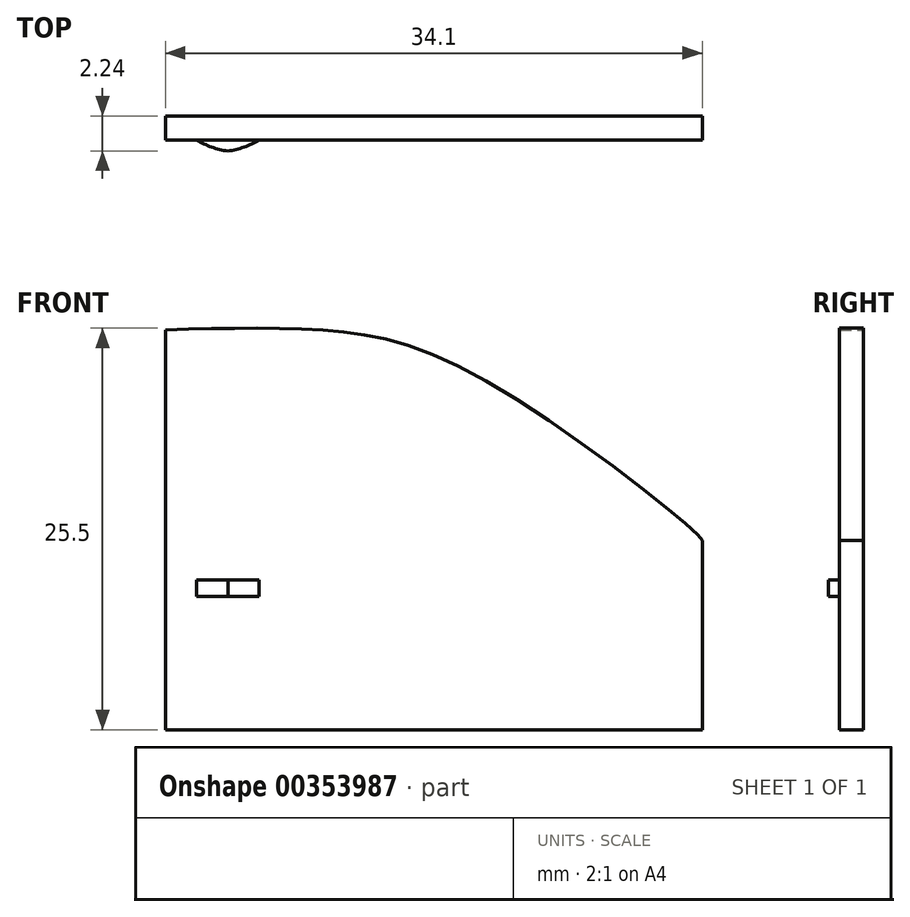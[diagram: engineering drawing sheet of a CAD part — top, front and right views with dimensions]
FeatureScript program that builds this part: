
annotation { "Feature Type Name" : "Feature", "Feature Type Description" : "" }
export const myFeature = defineFeature(function(context is Context, id is Id, definition is map)
    precondition{}
    {
        {
            var Q0;
            Q0=qCreatedBy(makeId("Front.planeOp"),FACE);
            var sketch = newSketch(context, id + "F0", { "sketchPlane" : qUnion([Q0])});
            skLineSegment(sketch, "E0", {"start": v(-20.5, 13.38) * mm, "end": v(-20.5, -12.02) * mm});
            skFitSpline(sketch, "E1", {"points": [v(-20.5, 13.38) * mm, v(-10.84, 13.38) * mm, v(0, 10.05) * mm, v(13.6, 0) * mm, v(13.4, 0) * mm], "startDerivative": vector(35.26, 0.94) * mm, "endDerivative": vector(-7.23, 1.73) * mm});
            skLineSegment(sketch, "E2", {"start": v(-20.5, -12.02) * mm, "end": v(13.6, -12.02) * mm});
            skLineSegment(sketch, "E3", {"start": v(13.6, -12.02) * mm, "end": v(13.6, 0) * mm});
            skLineSegment(sketch, "E4", {"start": v(13.6, 0) * mm, "end": v(-20.5, 0) * mm});
            skLineSegment(sketch, "E5.bottom", {"start": v(-18.52, -2.5) * mm, "end": v(-14.55, -2.5) * mm});
            skLineSegment(sketch, "E5.top", {"start": v(-18.52, -3.55) * mm, "end": v(-14.55, -3.55) * mm});
            skLineSegment(sketch, "E5.left", {"start": v(-18.52, -2.5) * mm, "end": v(-18.52, -3.55) * mm});
            skLineSegment(sketch, "E5.right", {"start": v(-14.55, -2.5) * mm, "end": v(-14.55, -3.55) * mm});
            skSolve(sketch);
        }
        {
            var Q0;
            {var subQ0=sQuery(id+"F0.wireOp",EDGE,"nOc6ndhr-CEWs-2MWZ-xoqL-Ha6ft26fFmGs");var subQ1=sQuery(id+"F0.wireOp",EDGE,"E4");var subQ2=makeQuery(id+"F0.imprint","INTERSECT",VERTEX,{"derivedFrom":[subQ1,subQ0]});Q0=makeQuery(id+"F0.imprint","IMPRINT",FACE,{"disambiguationData":[TD([[makeQuery(id+"F0.imprint","IMPRINT",EDGE,{"disambiguationData":[TD([[subQ2,1.0]])],"derivedFrom":subQ1}),-1.0]])]});}
            var Q1;
            {var subQ0=sQuery(id+"F0.wireOp",EDGE,"8BRhcVoK-4ZSY-d9QQ-jCl1-HMr4gjxtuWuF");var subQ1=sQuery(id+"F0.wireOp",EDGE,"XEESbgik-Cwhb-kf8o-8iuY-mVMpAegihUSW");var subQ2=makeQuery(id+"F0.imprint","INTERSECT",VERTEX,{"derivedFrom":[subQ1,subQ0]});Q1=makeQuery(id+"F0.imprint","IMPRINT",FACE,{"disambiguationData":[TD([[makeQuery(id+"F0.imprint","IMPRINT",EDGE,{"disambiguationData":[TD([[subQ2,-1.0]])],"derivedFrom":subQ1}),1.0]])]});}
            var Q2;
            {var subQ0=sQuery(id+"F0.wireOp",EDGE,"pVUgloD8-eKz4-1CY4-ZZar-P1BLLFPWEFhO");var subQ1=sQuery(id+"F0.wireOp",EDGE,"E1");var subQ2=makeQuery(id+"F0.imprint","INTERSECT",VERTEX,{"derivedFrom":[subQ1,subQ0]});Q2=makeQuery(id+"F0.imprint","IMPRINT",FACE,{"disambiguationData":[TD([[makeQuery(id+"F0.imprint","IMPRINT",EDGE,{"disambiguationData":[TD([[subQ2,1.0]])],"derivedFrom":subQ1}),-1.0]])]});}
            var Q3;
            {var subQ0=sQuery(id+"F0.wireOp",EDGE,"MwFNBffj-ykpu-HGD8-Ynrz-I9LzijhiDSCR");var subQ1=sQuery(id+"F0.wireOp",EDGE,"CX13CTTp-Oqm4-u2hn-fSbW-toaxqpDcd6P2");var subQ2=makeQuery(id+"F0.imprint","INTERSECT",VERTEX,{"derivedFrom":[subQ1,subQ0]});Q3=makeQuery(id+"F0.imprint","IMPRINT",FACE,{"disambiguationData":[TD([[makeQuery(id+"F0.imprint","IMPRINT",EDGE,{"disambiguationData":[TD([[subQ2,-1.0]])],"derivedFrom":subQ1}),1.0]])]});}
            var Q4;
            {var subQ0=sQuery(id+"F0.wireOp",EDGE,"8BRhcVoK-4ZSY-d9QQ-jCl1-HMr4gjxtuWuF");var subQ1=sQuery(id+"F0.wireOp",EDGE,"E0");var subQ2=makeQuery(id+"F0.imprint","INTERSECT",VERTEX,{"derivedFrom":[subQ1,subQ0]});Q4=makeQuery(id+"F0.imprint","IMPRINT",FACE,{"disambiguationData":[TD([[makeQuery(id+"F0.imprint","IMPRINT",EDGE,{"disambiguationData":[TD([[subQ2,-1.0]])],"derivedFrom":subQ1}),1.0]])]});}
            var Q5;
            {var subQ0=sQuery(id+"F0.wireOp",EDGE,"ATKICQp3-aMIP-nDqe-qzJb-LSgsvSxOWsnF");var subQ1=sQuery(id+"F0.wireOp",EDGE,"CX13CTTp-Oqm4-u2hn-fSbW-toaxqpDcd6P2");var subQ2=makeQuery(id+"F0.imprint","INTERSECT",VERTEX,{"derivedFrom":[subQ1,subQ0]});Q5=makeQuery(id+"F0.imprint","IMPRINT",FACE,{"disambiguationData":[TD([[makeQuery(id+"F0.imprint","IMPRINT",EDGE,{"disambiguationData":[TD([[subQ2,-1.0]])],"derivedFrom":subQ1}),1.0]])]});}
            var Q6;
            {var subQ0=sQuery(id+"F0.wireOp",EDGE,"MwFNBffj-ykpu-HGD8-Ynrz-I9LzijhiDSCR");var subQ1=sQuery(id+"F0.wireOp",EDGE,"XEESbgik-Cwhb-kf8o-8iuY-mVMpAegihUSW");var subQ2=makeQuery(id+"F0.imprint","INTERSECT",VERTEX,{"derivedFrom":[subQ1,subQ0]});Q6=makeQuery(id+"F0.imprint","IMPRINT",FACE,{"disambiguationData":[TD([[makeQuery(id+"F0.imprint","IMPRINT",EDGE,{"disambiguationData":[TD([[subQ2,-1.0]])],"derivedFrom":subQ1}),-1.0]])]});}
            var Q7;
            {var subQ0=sQuery(id+"F0.wireOp",EDGE,"XdJaFeX5-YPTi-reul-S0qf-juZpPkdLSGOt");var subQ1=sQuery(id+"F0.wireOp",EDGE,"XEESbgik-Cwhb-kf8o-8iuY-mVMpAegihUSW");var subQ2=makeQuery(id+"F0.imprint","INTERSECT",VERTEX,{"derivedFrom":[subQ1,subQ0]});Q7=makeQuery(id+"F0.imprint","IMPRINT",FACE,{"disambiguationData":[TD([[makeQuery(id+"F0.imprint","IMPRINT",EDGE,{"disambiguationData":[TD([[subQ2,-1.0]])],"derivedFrom":subQ1}),-1.0]])]});}
            var Q8;
            {var subQ0=sQuery(id+"F0.wireOp",EDGE,"ATKICQp3-aMIP-nDqe-qzJb-LSgsvSxOWsnF");var subQ1=sQuery(id+"F0.wireOp",EDGE,"E0");var subQ2=makeQuery(id+"F0.imprint","INTERSECT",VERTEX,{"derivedFrom":[subQ1,subQ0]});Q8=makeQuery(id+"F0.imprint","IMPRINT",FACE,{"disambiguationData":[TD([[makeQuery(id+"F0.imprint","IMPRINT",EDGE,{"disambiguationData":[TD([[subQ2,1.0]])],"derivedFrom":subQ1}),1.0]])]});}
            var Q9;
            {var subQ0=sQuery(id+"F0.wireOp",EDGE,"ATKICQp3-aMIP-nDqe-qzJb-LSgsvSxOWsnF");var subQ1=sQuery(id+"F0.wireOp",EDGE,"E0");var subQ2=makeQuery(id+"F0.imprint","INTERSECT",VERTEX,{"derivedFrom":[subQ1,subQ0]});Q9=makeQuery(id+"F0.imprint","IMPRINT",FACE,{"disambiguationData":[TD([[makeQuery(id+"F0.imprint","IMPRINT",EDGE,{"disambiguationData":[TD([[subQ2,-1.0]])],"derivedFrom":subQ1}),1.0]])]});}
            var Q10;
            {var subQ0=sQuery(id+"F0.wireOp",EDGE,"8BRhcVoK-4ZSY-d9QQ-jCl1-HMr4gjxtuWuF");var subQ1=sQuery(id+"F0.wireOp",EDGE,"yqfY02yN-hyVq-32UO-ZW3n-jwWNOL1hSBTT");var subQ2=makeQuery(id+"F0.imprint","INTERSECT",VERTEX,{"derivedFrom":[subQ1,subQ0]});Q10=makeQuery(id+"F0.imprint","IMPRINT",FACE,{"disambiguationData":[TD([[makeQuery(id+"F0.imprint","IMPRINT",EDGE,{"disambiguationData":[TD([[subQ2,-1.0]])],"derivedFrom":subQ1}),1.0]])]});}
            var Q11;
            {var subQ0=sQuery(id+"F0.wireOp",EDGE,"XdJaFeX5-YPTi-reul-S0qf-juZpPkdLSGOt");var subQ1=sQuery(id+"F0.wireOp",EDGE,"CX13CTTp-Oqm4-u2hn-fSbW-toaxqpDcd6P2");var subQ2=makeQuery(id+"F0.imprint","INTERSECT",VERTEX,{"derivedFrom":[subQ1,subQ0]});Q11=makeQuery(id+"F0.imprint","IMPRINT",FACE,{"disambiguationData":[TD([[makeQuery(id+"F0.imprint","IMPRINT",EDGE,{"disambiguationData":[TD([[subQ2,-1.0]])],"derivedFrom":subQ1}),1.0]])]});}
            var Q12;
            {var subQ1=sQuery(id+"F0.wireOp",EDGE,"E4");var subQ5=sQuery(id+"F0.wireOp",EDGE,"E1");var subQ6=makeQuery(id+"F0.imprint","INTERSECT",VERTEX,{"derivedFrom":[subQ5,subQ1]});Q12=makeQuery(id+"F0.imprint","IMPRINT",FACE,{"disambiguationData":[TD([[makeQuery(id+"F0.imprint","IMPRINT",EDGE,{"disambiguationData":[TD([[subQ6,-1.0]])],"derivedFrom":subQ1}),-1.0]])]});}
            var Q13;
            {var subQ0=sQuery(id+"F0.wireOp",EDGE,"ONkRjr3D-5ST7-0iBJ-Hq3S-bNWUPIyy0om7");var subQ1=sQuery(id+"F0.wireOp",EDGE,"E0");var subQ2=makeQuery(id+"F0.imprint","INTERSECT",VERTEX,{"derivedFrom":[subQ1,subQ0]});Q13=makeQuery(id+"F0.imprint","IMPRINT",FACE,{"disambiguationData":[TD([[makeQuery(id+"F0.imprint","IMPRINT",EDGE,{"disambiguationData":[TD([[subQ2,-1.0]])],"derivedFrom":subQ1}),1.0]])]});}
            var Q14;
            {var subQ0=sQuery(id+"F0.wireOp",EDGE,"gvejoAXR-BtHd-F8Sq-gFUB-eTjeAkh79I8N");var subQ1=sQuery(id+"F0.wireOp",EDGE,"PEqbovu0-osZd-sZTq-e7nW-4YB9cD3i2QqJ");var subQ2=makeQuery(id+"F0.imprint","INTERSECT",VERTEX,{"derivedFrom":[subQ1,subQ0]});Q14=makeQuery(id+"F0.imprint","IMPRINT",FACE,{"disambiguationData":[TD([[makeQuery(id+"F0.imprint","IMPRINT",EDGE,{"disambiguationData":[TD([[subQ2,-1.0]])],"derivedFrom":subQ1}),1.0]])]});}
            var Q15;
            {var subQ0=sQuery(id+"F0.wireOp",EDGE,"XEESbgik-Cwhb-kf8o-8iuY-mVMpAegihUSW");var subQ1=sQuery(id+"F0.wireOp",EDGE,"E1");var subQ2=makeQuery(id+"F0.imprint","INTERSECT",VERTEX,{"derivedFrom":[subQ1,subQ0]});Q15=makeQuery(id+"F0.imprint","IMPRINT",FACE,{"disambiguationData":[TD([[makeQuery(id+"F0.imprint","IMPRINT",EDGE,{"disambiguationData":[TD([[subQ2,-1.0]])],"derivedFrom":subQ1}),-1.0]])]});}
            var Q16;
            {var subQ0=sQuery(id+"F0.wireOp",EDGE,"ONkRjr3D-5ST7-0iBJ-Hq3S-bNWUPIyy0om7");var subQ1=sQuery(id+"F0.wireOp",EDGE,"V6lheY5w-4WYN-of84-aoai-MSi1px95FpYR");var subQ2=makeQuery(id+"F0.imprint","INTERSECT",VERTEX,{"derivedFrom":[subQ1,subQ0]});Q16=makeQuery(id+"F0.imprint","IMPRINT",FACE,{"disambiguationData":[TD([[makeQuery(id+"F0.imprint","IMPRINT",EDGE,{"disambiguationData":[TD([[subQ2,-1.0]])],"derivedFrom":subQ1}),1.0]])]});}
            var Q17;
            {var subQ0=sQuery(id+"F0.wireOp",EDGE,"8BRhcVoK-4ZSY-d9QQ-jCl1-HMr4gjxtuWuF");var subQ1=sQuery(id+"F0.wireOp",EDGE,"V6lheY5w-4WYN-of84-aoai-MSi1px95FpYR");var subQ2=makeQuery(id+"F0.imprint","INTERSECT",VERTEX,{"derivedFrom":[subQ1,subQ0]});Q17=makeQuery(id+"F0.imprint","IMPRINT",FACE,{"disambiguationData":[TD([[makeQuery(id+"F0.imprint","IMPRINT",EDGE,{"disambiguationData":[TD([[subQ2,-1.0]])],"derivedFrom":subQ1}),1.0]])]});}
            var Q18;
            {var subQ0=sQuery(id+"F0.wireOp",EDGE,"ATKICQp3-aMIP-nDqe-qzJb-LSgsvSxOWsnF");var subQ1=sQuery(id+"F0.wireOp",EDGE,"V6lheY5w-4WYN-of84-aoai-MSi1px95FpYR");var subQ2=makeQuery(id+"F0.imprint","INTERSECT",VERTEX,{"derivedFrom":[subQ1,subQ0]});Q18=makeQuery(id+"F0.imprint","IMPRINT",FACE,{"disambiguationData":[TD([[makeQuery(id+"F0.imprint","IMPRINT",EDGE,{"disambiguationData":[TD([[subQ2,-1.0]])],"derivedFrom":subQ1}),1.0]])]});}
            var Q19;
            {var subQ0=sQuery(id+"F0.wireOp",EDGE,"ONkRjr3D-5ST7-0iBJ-Hq3S-bNWUPIyy0om7");var subQ1=sQuery(id+"F0.wireOp",EDGE,"yqfY02yN-hyVq-32UO-ZW3n-jwWNOL1hSBTT");var subQ2=makeQuery(id+"F0.imprint","INTERSECT",VERTEX,{"derivedFrom":[subQ1,subQ0]});Q19=makeQuery(id+"F0.imprint","IMPRINT",FACE,{"disambiguationData":[TD([[makeQuery(id+"F0.imprint","IMPRINT",EDGE,{"disambiguationData":[TD([[subQ2,-1.0]])],"derivedFrom":subQ1}),1.0]])]});}
            var Q20;
            {var subQ0=sQuery(id+"F0.wireOp",EDGE,"MwFNBffj-ykpu-HGD8-Ynrz-I9LzijhiDSCR");var subQ1=sQuery(id+"F0.wireOp",EDGE,"E0");var subQ2=makeQuery(id+"F0.imprint","INTERSECT",VERTEX,{"derivedFrom":[subQ1,subQ0]});Q20=makeQuery(id+"F0.imprint","IMPRINT",FACE,{"disambiguationData":[TD([[makeQuery(id+"F0.imprint","IMPRINT",EDGE,{"disambiguationData":[TD([[subQ2,-1.0]])],"derivedFrom":subQ1}),1.0]])]});}
            var Q21;
            {var subQ0=sQuery(id+"F0.wireOp",EDGE,"XdJaFeX5-YPTi-reul-S0qf-juZpPkdLSGOt");var subQ1=sQuery(id+"F0.wireOp",EDGE,"E1");var subQ2=makeQuery(id+"F0.imprint","INTERSECT",VERTEX,{"derivedFrom":[subQ1,subQ0]});Q21=makeQuery(id+"F0.imprint","IMPRINT",FACE,{"disambiguationData":[TD([[makeQuery(id+"F0.imprint","IMPRINT",EDGE,{"disambiguationData":[TD([[subQ2,-1.0]])],"derivedFrom":subQ1}),-1.0]])]});}
            var Q22;
            {var subQ0=sQuery(id+"F0.wireOp",EDGE,"Okv4lNKS-qbql-g7VV-lbg5-xwRJb0XAX9qC");var subQ1=sQuery(id+"F0.wireOp",EDGE,"E0");var subQ2=makeQuery(id+"F0.imprint","INTERSECT",VERTEX,{"derivedFrom":[subQ1,subQ0]});Q22=makeQuery(id+"F0.imprint","IMPRINT",FACE,{"disambiguationData":[TD([[makeQuery(id+"F0.imprint","IMPRINT",EDGE,{"disambiguationData":[TD([[subQ2,-1.0]])],"derivedFrom":subQ1}),1.0]])]});}
            var Q23;
            {var subQ0=sQuery(id+"F0.wireOp",EDGE,"XdJaFeX5-YPTi-reul-S0qf-juZpPkdLSGOt");var subQ1=sQuery(id+"F0.wireOp",EDGE,"E0");var subQ2=makeQuery(id+"F0.imprint","INTERSECT",VERTEX,{"derivedFrom":[subQ1,subQ0]});Q23=makeQuery(id+"F0.imprint","IMPRINT",FACE,{"disambiguationData":[TD([[makeQuery(id+"F0.imprint","IMPRINT",EDGE,{"disambiguationData":[TD([[subQ2,-1.0]])],"derivedFrom":subQ1}),1.0]])]});}
            var Q24;
            {var subQ0=sQuery(id+"F0.wireOp",EDGE,"gvejoAXR-BtHd-F8Sq-gFUB-eTjeAkh79I8N");var subQ1=sQuery(id+"F0.wireOp",EDGE,"CX13CTTp-Oqm4-u2hn-fSbW-toaxqpDcd6P2");var subQ2=makeQuery(id+"F0.imprint","INTERSECT",VERTEX,{"derivedFrom":[subQ1,subQ0]});Q24=makeQuery(id+"F0.imprint","IMPRINT",FACE,{"disambiguationData":[TD([[makeQuery(id+"F0.imprint","IMPRINT",EDGE,{"disambiguationData":[TD([[subQ2,-1.0]])],"derivedFrom":subQ1}),1.0]])]});}
            var Q25;
            {var subQ0=sQuery(id+"F0.wireOp",EDGE,"8BRhcVoK-4ZSY-d9QQ-jCl1-HMr4gjxtuWuF");var subQ1=sQuery(id+"F0.wireOp",EDGE,"XEESbgik-Cwhb-kf8o-8iuY-mVMpAegihUSW");var subQ2=makeQuery(id+"F0.imprint","INTERSECT",VERTEX,{"derivedFrom":[subQ1,subQ0]});Q25=makeQuery(id+"F0.imprint","IMPRINT",FACE,{"disambiguationData":[TD([[makeQuery(id+"F0.imprint","IMPRINT",EDGE,{"disambiguationData":[TD([[subQ2,-1.0]])],"derivedFrom":subQ1}),-1.0]])]});}
            var Q26;
            {var subQ0=sQuery(id+"F0.wireOp",EDGE,"Okv4lNKS-qbql-g7VV-lbg5-xwRJb0XAX9qC");var subQ1=sQuery(id+"F0.wireOp",EDGE,"E1");var subQ2=makeQuery(id+"F0.imprint","INTERSECT",VERTEX,{"derivedFrom":[subQ1,subQ0]});Q26=makeQuery(id+"F0.imprint","IMPRINT",FACE,{"disambiguationData":[TD([[makeQuery(id+"F0.imprint","IMPRINT",EDGE,{"disambiguationData":[TD([[subQ2,-1.0]])],"derivedFrom":subQ1}),-1.0]])]});}
            var Q27;
            {var subQ1=sQuery(id+"F0.wireOp",EDGE,"E1");var subQ5=sQuery(id+"F0.wireOp",EDGE,"fXT5uzoG-60Do-cvdt-QS0y-XCeuEJHzKh4q");var subQ6=makeQuery(id+"F0.imprint","INTERSECT",VERTEX,{"derivedFrom":[subQ1,subQ5]});Q27=makeQuery(id+"F0.imprint","IMPRINT",FACE,{"disambiguationData":[TD([[makeQuery(id+"F0.imprint","IMPRINT",EDGE,{"disambiguationData":[TD([[subQ6,1.0]])],"derivedFrom":subQ1}),-1.0]])]});}
            var Q28;
            {var subQ0=sQuery(id+"F0.wireOp",EDGE,"BWVHoUEd-ofww-dxFT-yNqJ-OOrmRnXLyRp3");var subQ1=sQuery(id+"F0.wireOp",EDGE,"E0");var subQ2=makeQuery(id+"F0.imprint","INTERSECT",VERTEX,{"derivedFrom":[subQ1,subQ0]});Q28=makeQuery(id+"F0.imprint","IMPRINT",FACE,{"disambiguationData":[TD([[makeQuery(id+"F0.imprint","IMPRINT",EDGE,{"disambiguationData":[TD([[subQ2,-1.0]])],"derivedFrom":subQ1}),1.0]])]});}
            var Q29;
            {var subQ0=sQuery(id+"F0.wireOp",EDGE,"E4");var subQ1=sQuery(id+"F0.wireOp",EDGE,"E0");var subQ2=makeQuery(id+"F0.imprint","INTERSECT",VERTEX,{"derivedFrom":[subQ1,subQ0]});Q29=makeQuery(id+"F0.imprint","IMPRINT",FACE,{"disambiguationData":[TD([[makeQuery(id+"F0.imprint","IMPRINT",EDGE,{"disambiguationData":[TD([[subQ2,1.0]])],"derivedFrom":subQ1}),1.0]])]});}
            var Q30;
            {var subQ0=sQuery(id+"F0.wireOp",EDGE,"Okv4lNKS-qbql-g7VV-lbg5-xwRJb0XAX9qC");var subQ1=sQuery(id+"F0.wireOp",EDGE,"XEESbgik-Cwhb-kf8o-8iuY-mVMpAegihUSW");var subQ2=makeQuery(id+"F0.imprint","INTERSECT",VERTEX,{"derivedFrom":[subQ1,subQ0]});Q30=makeQuery(id+"F0.imprint","IMPRINT",FACE,{"disambiguationData":[TD([[makeQuery(id+"F0.imprint","IMPRINT",EDGE,{"disambiguationData":[TD([[subQ2,-1.0]])],"derivedFrom":subQ1}),1.0]])]});}
            var Q31;
            {var subQ0=sQuery(id+"F0.wireOp",EDGE,"BWVHoUEd-ofww-dxFT-yNqJ-OOrmRnXLyRp3");var subQ1=sQuery(id+"F0.wireOp",EDGE,"yqfY02yN-hyVq-32UO-ZW3n-jwWNOL1hSBTT");var subQ2=makeQuery(id+"F0.imprint","INTERSECT",VERTEX,{"derivedFrom":[subQ1,subQ0]});Q31=makeQuery(id+"F0.imprint","IMPRINT",FACE,{"disambiguationData":[TD([[makeQuery(id+"F0.imprint","IMPRINT",EDGE,{"disambiguationData":[TD([[subQ2,-1.0]])],"derivedFrom":subQ1}),1.0]])]});}
            var Q32;
            {var subQ0=sQuery(id+"F0.wireOp",EDGE,"ONkRjr3D-5ST7-0iBJ-Hq3S-bNWUPIyy0om7");var subQ1=sQuery(id+"F0.wireOp",EDGE,"E1");var subQ2=makeQuery(id+"F0.imprint","INTERSECT",VERTEX,{"derivedFrom":[subQ1,subQ0]});Q32=makeQuery(id+"F0.imprint","IMPRINT",FACE,{"disambiguationData":[TD([[makeQuery(id+"F0.imprint","IMPRINT",EDGE,{"disambiguationData":[TD([[subQ2,-1.0]])],"derivedFrom":subQ1}),-1.0]])]});}
            var Q33;
            {var subQ0=sQuery(id+"F0.wireOp",EDGE,"BWVHoUEd-ofww-dxFT-yNqJ-OOrmRnXLyRp3");var subQ1=sQuery(id+"F0.wireOp",EDGE,"CX13CTTp-Oqm4-u2hn-fSbW-toaxqpDcd6P2");var subQ2=makeQuery(id+"F0.imprint","INTERSECT",VERTEX,{"derivedFrom":[subQ1,subQ0]});Q33=makeQuery(id+"F0.imprint","IMPRINT",FACE,{"disambiguationData":[TD([[makeQuery(id+"F0.imprint","IMPRINT",EDGE,{"disambiguationData":[TD([[subQ2,-1.0]])],"derivedFrom":subQ1}),1.0]])]});}
            var Q34;
            {var subQ0=sQuery(id+"F0.wireOp",EDGE,"Okv4lNKS-qbql-g7VV-lbg5-xwRJb0XAX9qC");var subQ1=sQuery(id+"F0.wireOp",EDGE,"nOc6ndhr-CEWs-2MWZ-xoqL-Ha6ft26fFmGs");var subQ2=makeQuery(id+"F0.imprint","INTERSECT",VERTEX,{"derivedFrom":[subQ1,subQ0]});Q34=makeQuery(id+"F0.imprint","IMPRINT",FACE,{"disambiguationData":[TD([[makeQuery(id+"F0.imprint","IMPRINT",EDGE,{"disambiguationData":[TD([[subQ2,-1.0]])],"derivedFrom":subQ1}),1.0]])]});}
            var Q35;
            {var subQ0=sQuery(id+"F0.wireOp",EDGE,"BWVHoUEd-ofww-dxFT-yNqJ-OOrmRnXLyRp3");var subQ1=sQuery(id+"F0.wireOp",EDGE,"nOc6ndhr-CEWs-2MWZ-xoqL-Ha6ft26fFmGs");var subQ2=makeQuery(id+"F0.imprint","INTERSECT",VERTEX,{"derivedFrom":[subQ1,subQ0]});Q35=makeQuery(id+"F0.imprint","IMPRINT",FACE,{"disambiguationData":[TD([[makeQuery(id+"F0.imprint","IMPRINT",EDGE,{"disambiguationData":[TD([[subQ2,-1.0]])],"derivedFrom":subQ1}),1.0]])]});}
            var Q36;
            {var subQ0=sQuery(id+"F0.wireOp",EDGE,"ONkRjr3D-5ST7-0iBJ-Hq3S-bNWUPIyy0om7");var subQ1=sQuery(id+"F0.wireOp",EDGE,"PEqbovu0-osZd-sZTq-e7nW-4YB9cD3i2QqJ");var subQ2=makeQuery(id+"F0.imprint","INTERSECT",VERTEX,{"derivedFrom":[subQ1,subQ0]});Q36=makeQuery(id+"F0.imprint","IMPRINT",FACE,{"disambiguationData":[TD([[makeQuery(id+"F0.imprint","IMPRINT",EDGE,{"disambiguationData":[TD([[subQ2,-1.0]])],"derivedFrom":subQ1}),1.0]])]});}
            var Q37;
            {var subQ0=sQuery(id+"F0.wireOp",EDGE,"gvejoAXR-BtHd-F8Sq-gFUB-eTjeAkh79I8N");var subQ1=sQuery(id+"F0.wireOp",EDGE,"XEESbgik-Cwhb-kf8o-8iuY-mVMpAegihUSW");var subQ2=makeQuery(id+"F0.imprint","INTERSECT",VERTEX,{"derivedFrom":[subQ1,subQ0]});Q37=makeQuery(id+"F0.imprint","IMPRINT",FACE,{"disambiguationData":[TD([[makeQuery(id+"F0.imprint","IMPRINT",EDGE,{"disambiguationData":[TD([[subQ2,-1.0]])],"derivedFrom":subQ1}),-1.0]])]});}
            var Q38;
            {var subQ0=sQuery(id+"F0.wireOp",EDGE,"V6lheY5w-4WYN-of84-aoai-MSi1px95FpYR");var subQ1=sQuery(id+"F0.wireOp",EDGE,"E4");var subQ2=makeQuery(id+"F0.imprint","INTERSECT",VERTEX,{"derivedFrom":[subQ1,subQ0]});Q38=makeQuery(id+"F0.imprint","IMPRINT",FACE,{"disambiguationData":[TD([[makeQuery(id+"F0.imprint","IMPRINT",EDGE,{"disambiguationData":[TD([[subQ2,1.0]])],"derivedFrom":subQ1}),-1.0]])]});}
            var Q39;
            {var subQ0=sQuery(id+"F0.wireOp",EDGE,"XdJaFeX5-YPTi-reul-S0qf-juZpPkdLSGOt");var subQ1=sQuery(id+"F0.wireOp",EDGE,"XEESbgik-Cwhb-kf8o-8iuY-mVMpAegihUSW");var subQ2=makeQuery(id+"F0.imprint","INTERSECT",VERTEX,{"derivedFrom":[subQ1,subQ0]});Q39=makeQuery(id+"F0.imprint","IMPRINT",FACE,{"disambiguationData":[TD([[makeQuery(id+"F0.imprint","IMPRINT",EDGE,{"disambiguationData":[TD([[subQ2,-1.0]])],"derivedFrom":subQ1}),1.0]])]});}
            var Q40;
            {var subQ0=sQuery(id+"F0.wireOp",EDGE,"CX13CTTp-Oqm4-u2hn-fSbW-toaxqpDcd6P2");var subQ1=sQuery(id+"F0.wireOp",EDGE,"E4");var subQ2=makeQuery(id+"F0.imprint","INTERSECT",VERTEX,{"derivedFrom":[subQ1,subQ0]});Q40=makeQuery(id+"F0.imprint","IMPRINT",FACE,{"disambiguationData":[TD([[makeQuery(id+"F0.imprint","IMPRINT",EDGE,{"disambiguationData":[TD([[subQ2,1.0]])],"derivedFrom":subQ1}),-1.0]])]});}
            var Q41;
            {var subQ0=sQuery(id+"F0.wireOp",EDGE,"YQxu8z3E-p7so-N4Wg-IzPX-PEhLxJgFoJVr");var subQ1=sQuery(id+"F0.wireOp",EDGE,"E4");var subQ2=makeQuery(id+"F0.imprint","INTERSECT",VERTEX,{"derivedFrom":[subQ1,subQ0]});Q41=makeQuery(id+"F0.imprint","IMPRINT",FACE,{"disambiguationData":[TD([[makeQuery(id+"F0.imprint","IMPRINT",EDGE,{"disambiguationData":[TD([[subQ2,1.0]])],"derivedFrom":subQ1}),-1.0]])]});}
            var Q42;
            {var subQ0=sQuery(id+"F0.wireOp",EDGE,"ONkRjr3D-5ST7-0iBJ-Hq3S-bNWUPIyy0om7");var subQ1=sQuery(id+"F0.wireOp",EDGE,"XEESbgik-Cwhb-kf8o-8iuY-mVMpAegihUSW");var subQ2=makeQuery(id+"F0.imprint","INTERSECT",VERTEX,{"derivedFrom":[subQ1,subQ0]});Q42=makeQuery(id+"F0.imprint","IMPRINT",FACE,{"disambiguationData":[TD([[makeQuery(id+"F0.imprint","IMPRINT",EDGE,{"disambiguationData":[TD([[subQ2,-1.0]])],"derivedFrom":subQ1}),-1.0]])]});}
            var Q43;
            {var subQ0=sQuery(id+"F0.wireOp",EDGE,"E1");var subQ1=sQuery(id+"F0.wireOp",EDGE,"E0");var subQ2=makeQuery(id+"F0.imprint","INTERSECT",VERTEX,{"derivedFrom":[subQ1,subQ0]});Q43=makeQuery(id+"F0.imprint","IMPRINT",FACE,{"disambiguationData":[TD([[makeQuery(id+"F0.imprint","IMPRINT",EDGE,{"disambiguationData":[TD([[subQ2,-1.0]])],"derivedFrom":subQ1}),1.0]])]});}
            var Q44;
            {var subQ0=sQuery(id+"F0.wireOp",EDGE,"XEESbgik-Cwhb-kf8o-8iuY-mVMpAegihUSW");var subQ1=sQuery(id+"F0.wireOp",EDGE,"E1");var subQ2=makeQuery(id+"F0.imprint","INTERSECT",VERTEX,{"derivedFrom":[subQ1,subQ0]});Q44=makeQuery(id+"F0.imprint","IMPRINT",FACE,{"disambiguationData":[TD([[makeQuery(id+"F0.imprint","IMPRINT",EDGE,{"disambiguationData":[TD([[subQ2,1.0]])],"derivedFrom":subQ1}),-1.0]])]});}
            var Q45;
            {var subQ0=sQuery(id+"F0.wireOp",EDGE,"8BRhcVoK-4ZSY-d9QQ-jCl1-HMr4gjxtuWuF");var subQ1=sQuery(id+"F0.wireOp",EDGE,"PEqbovu0-osZd-sZTq-e7nW-4YB9cD3i2QqJ");var subQ2=makeQuery(id+"F0.imprint","INTERSECT",VERTEX,{"derivedFrom":[subQ1,subQ0]});Q45=makeQuery(id+"F0.imprint","IMPRINT",FACE,{"disambiguationData":[TD([[makeQuery(id+"F0.imprint","IMPRINT",EDGE,{"disambiguationData":[TD([[subQ2,-1.0]])],"derivedFrom":subQ1}),1.0]])]});}
            var Q46;
            {var subQ0=sQuery(id+"F0.wireOp",EDGE,"PEqbovu0-osZd-sZTq-e7nW-4YB9cD3i2QqJ");var subQ1=sQuery(id+"F0.wireOp",EDGE,"E4");var subQ2=makeQuery(id+"F0.imprint","INTERSECT",VERTEX,{"derivedFrom":[subQ1,subQ0]});Q46=makeQuery(id+"F0.imprint","IMPRINT",FACE,{"disambiguationData":[TD([[makeQuery(id+"F0.imprint","IMPRINT",EDGE,{"disambiguationData":[TD([[subQ2,1.0]])],"derivedFrom":subQ1}),-1.0]])]});}
            var Q47;
            {var subQ0=sQuery(id+"F0.wireOp",EDGE,"ATKICQp3-aMIP-nDqe-qzJb-LSgsvSxOWsnF");var subQ1=sQuery(id+"F0.wireOp",EDGE,"XEESbgik-Cwhb-kf8o-8iuY-mVMpAegihUSW");var subQ2=makeQuery(id+"F0.imprint","INTERSECT",VERTEX,{"derivedFrom":[subQ1,subQ0]});Q47=makeQuery(id+"F0.imprint","IMPRINT",FACE,{"disambiguationData":[TD([[makeQuery(id+"F0.imprint","IMPRINT",EDGE,{"disambiguationData":[TD([[subQ2,-1.0]])],"derivedFrom":subQ1}),1.0]])]});}
            var Q48;
            {var subQ0=sQuery(id+"F0.wireOp",EDGE,"Okv4lNKS-qbql-g7VV-lbg5-xwRJb0XAX9qC");var subQ1=sQuery(id+"F0.wireOp",EDGE,"XEESbgik-Cwhb-kf8o-8iuY-mVMpAegihUSW");var subQ2=makeQuery(id+"F0.imprint","INTERSECT",VERTEX,{"derivedFrom":[subQ1,subQ0]});Q48=makeQuery(id+"F0.imprint","IMPRINT",FACE,{"disambiguationData":[TD([[makeQuery(id+"F0.imprint","IMPRINT",EDGE,{"disambiguationData":[TD([[subQ2,-1.0]])],"derivedFrom":subQ1}),-1.0]])]});}
            var Q49;
            {var subQ0=sQuery(id+"F0.wireOp",EDGE,"MwFNBffj-ykpu-HGD8-Ynrz-I9LzijhiDSCR");var subQ1=sQuery(id+"F0.wireOp",EDGE,"XEESbgik-Cwhb-kf8o-8iuY-mVMpAegihUSW");var subQ2=makeQuery(id+"F0.imprint","INTERSECT",VERTEX,{"derivedFrom":[subQ1,subQ0]});Q49=makeQuery(id+"F0.imprint","IMPRINT",FACE,{"disambiguationData":[TD([[makeQuery(id+"F0.imprint","IMPRINT",EDGE,{"disambiguationData":[TD([[subQ2,-1.0]])],"derivedFrom":subQ1}),1.0]])]});}
            var Q50;
            {var subQ0=sQuery(id+"F0.wireOp",EDGE,"MwFNBffj-ykpu-HGD8-Ynrz-I9LzijhiDSCR");var subQ1=sQuery(id+"F0.wireOp",EDGE,"PEqbovu0-osZd-sZTq-e7nW-4YB9cD3i2QqJ");var subQ2=makeQuery(id+"F0.imprint","INTERSECT",VERTEX,{"derivedFrom":[subQ1,subQ0]});Q50=makeQuery(id+"F0.imprint","IMPRINT",FACE,{"disambiguationData":[TD([[makeQuery(id+"F0.imprint","IMPRINT",EDGE,{"disambiguationData":[TD([[subQ2,-1.0]])],"derivedFrom":subQ1}),1.0]])]});}
            var Q51;
            {var subQ0=sQuery(id+"F0.wireOp",EDGE,"Okv4lNKS-qbql-g7VV-lbg5-xwRJb0XAX9qC");var subQ1=sQuery(id+"F0.wireOp",EDGE,"yqfY02yN-hyVq-32UO-ZW3n-jwWNOL1hSBTT");var subQ2=makeQuery(id+"F0.imprint","INTERSECT",VERTEX,{"derivedFrom":[subQ1,subQ0]});Q51=makeQuery(id+"F0.imprint","IMPRINT",FACE,{"disambiguationData":[TD([[makeQuery(id+"F0.imprint","IMPRINT",EDGE,{"disambiguationData":[TD([[subQ2,-1.0]])],"derivedFrom":subQ1}),1.0]])]});}
            var Q52;
            {var subQ0=sQuery(id+"F0.wireOp",EDGE,"XdJaFeX5-YPTi-reul-S0qf-juZpPkdLSGOt");var subQ1=sQuery(id+"F0.wireOp",EDGE,"PEqbovu0-osZd-sZTq-e7nW-4YB9cD3i2QqJ");var subQ2=makeQuery(id+"F0.imprint","INTERSECT",VERTEX,{"derivedFrom":[subQ1,subQ0]});Q52=makeQuery(id+"F0.imprint","IMPRINT",FACE,{"disambiguationData":[TD([[makeQuery(id+"F0.imprint","IMPRINT",EDGE,{"disambiguationData":[TD([[subQ2,-1.0]])],"derivedFrom":subQ1}),1.0]])]});}
            var Q53;
            {var subQ0=sQuery(id+"F0.wireOp",EDGE,"MwFNBffj-ykpu-HGD8-Ynrz-I9LzijhiDSCR");var subQ1=sQuery(id+"F0.wireOp",EDGE,"E1");var subQ2=makeQuery(id+"F0.imprint","INTERSECT",VERTEX,{"derivedFrom":[subQ1,subQ0]});Q53=makeQuery(id+"F0.imprint","IMPRINT",FACE,{"disambiguationData":[TD([[makeQuery(id+"F0.imprint","IMPRINT",EDGE,{"disambiguationData":[TD([[subQ2,-1.0]])],"derivedFrom":subQ1}),-1.0]])]});}
            var Q54;
            {var subQ0=sQuery(id+"F0.wireOp",EDGE,"XdJaFeX5-YPTi-reul-S0qf-juZpPkdLSGOt");var subQ1=sQuery(id+"F0.wireOp",EDGE,"V6lheY5w-4WYN-of84-aoai-MSi1px95FpYR");var subQ2=makeQuery(id+"F0.imprint","INTERSECT",VERTEX,{"derivedFrom":[subQ1,subQ0]});Q54=makeQuery(id+"F0.imprint","IMPRINT",FACE,{"disambiguationData":[TD([[makeQuery(id+"F0.imprint","IMPRINT",EDGE,{"disambiguationData":[TD([[subQ2,-1.0]])],"derivedFrom":subQ1}),1.0]])]});}
            var Q55;
            {var subQ1=sQuery(id+"F0.wireOp",EDGE,"E1");var subQ5=sQuery(id+"F0.wireOp",EDGE,"YQxu8z3E-p7so-N4Wg-IzPX-PEhLxJgFoJVr");var subQ6=makeQuery(id+"F0.imprint","INTERSECT",VERTEX,{"derivedFrom":[subQ1,subQ5]});Q55=makeQuery(id+"F0.imprint","IMPRINT",FACE,{"disambiguationData":[TD([[makeQuery(id+"F0.imprint","IMPRINT",EDGE,{"disambiguationData":[TD([[subQ6,1.0]])],"derivedFrom":subQ1}),-1.0]])]});}
            var Q56;
            {var subQ0=sQuery(id+"F0.wireOp",EDGE,"ONkRjr3D-5ST7-0iBJ-Hq3S-bNWUPIyy0om7");var subQ1=sQuery(id+"F0.wireOp",EDGE,"CX13CTTp-Oqm4-u2hn-fSbW-toaxqpDcd6P2");var subQ2=makeQuery(id+"F0.imprint","INTERSECT",VERTEX,{"derivedFrom":[subQ1,subQ0]});Q56=makeQuery(id+"F0.imprint","IMPRINT",FACE,{"disambiguationData":[TD([[makeQuery(id+"F0.imprint","IMPRINT",EDGE,{"disambiguationData":[TD([[subQ2,-1.0]])],"derivedFrom":subQ1}),1.0]])]});}
            var Q57;
            {var subQ3=sQuery(id+"F0.wireOp",EDGE,"yqfY02yN-hyVq-32UO-ZW3n-jwWNOL1hSBTT");var subQ5=sQuery(id+"F0.wireOp",EDGE,"E1");var subQ6=makeQuery(id+"F0.imprint","INTERSECT",VERTEX,{"derivedFrom":[subQ5,subQ3]});Q57=makeQuery(id+"F0.imprint","IMPRINT",FACE,{"disambiguationData":[TD([[makeQuery(id+"F0.imprint","IMPRINT",EDGE,{"disambiguationData":[TD([[subQ6,1.0]])],"derivedFrom":subQ5}),-1.0]])]});}
            var Q58;
            {var subQ0=sQuery(id+"F0.wireOp",EDGE,"XdJaFeX5-YPTi-reul-S0qf-juZpPkdLSGOt");var subQ1=sQuery(id+"F0.wireOp",EDGE,"nOc6ndhr-CEWs-2MWZ-xoqL-Ha6ft26fFmGs");var subQ2=makeQuery(id+"F0.imprint","INTERSECT",VERTEX,{"derivedFrom":[subQ1,subQ0]});Q58=makeQuery(id+"F0.imprint","IMPRINT",FACE,{"disambiguationData":[TD([[makeQuery(id+"F0.imprint","IMPRINT",EDGE,{"disambiguationData":[TD([[subQ2,-1.0]])],"derivedFrom":subQ1}),1.0]])]});}
            var Q59;
            {var subQ0=sQuery(id+"F0.wireOp",EDGE,"Okv4lNKS-qbql-g7VV-lbg5-xwRJb0XAX9qC");var subQ1=sQuery(id+"F0.wireOp",EDGE,"V6lheY5w-4WYN-of84-aoai-MSi1px95FpYR");var subQ2=makeQuery(id+"F0.imprint","INTERSECT",VERTEX,{"derivedFrom":[subQ1,subQ0]});Q59=makeQuery(id+"F0.imprint","IMPRINT",FACE,{"disambiguationData":[TD([[makeQuery(id+"F0.imprint","IMPRINT",EDGE,{"disambiguationData":[TD([[subQ2,-1.0]])],"derivedFrom":subQ1}),1.0]])]});}
            var Q60;
            {var subQ0=sQuery(id+"F0.wireOp",EDGE,"Okv4lNKS-qbql-g7VV-lbg5-xwRJb0XAX9qC");var subQ1=sQuery(id+"F0.wireOp",EDGE,"PEqbovu0-osZd-sZTq-e7nW-4YB9cD3i2QqJ");var subQ2=makeQuery(id+"F0.imprint","INTERSECT",VERTEX,{"derivedFrom":[subQ1,subQ0]});Q60=makeQuery(id+"F0.imprint","IMPRINT",FACE,{"disambiguationData":[TD([[makeQuery(id+"F0.imprint","IMPRINT",EDGE,{"disambiguationData":[TD([[subQ2,-1.0]])],"derivedFrom":subQ1}),1.0]])]});}
            var Q61;
            {var subQ0=sQuery(id+"F0.wireOp",EDGE,"ATKICQp3-aMIP-nDqe-qzJb-LSgsvSxOWsnF");var subQ1=sQuery(id+"F0.wireOp",EDGE,"XEESbgik-Cwhb-kf8o-8iuY-mVMpAegihUSW");var subQ2=makeQuery(id+"F0.imprint","INTERSECT",VERTEX,{"derivedFrom":[subQ1,subQ0]});Q61=makeQuery(id+"F0.imprint","IMPRINT",FACE,{"disambiguationData":[TD([[makeQuery(id+"F0.imprint","IMPRINT",EDGE,{"disambiguationData":[TD([[subQ2,-1.0]])],"derivedFrom":subQ1}),-1.0]])]});}
            var Q62;
            {var subQ0=sQuery(id+"F0.wireOp",EDGE,"XEESbgik-Cwhb-kf8o-8iuY-mVMpAegihUSW");var subQ1=sQuery(id+"F0.wireOp",EDGE,"E4");var subQ2=makeQuery(id+"F0.imprint","INTERSECT",VERTEX,{"derivedFrom":[subQ1,subQ0]});Q62=makeQuery(id+"F0.imprint","IMPRINT",FACE,{"disambiguationData":[TD([[makeQuery(id+"F0.imprint","IMPRINT",EDGE,{"disambiguationData":[TD([[subQ2,1.0]])],"derivedFrom":subQ1}),-1.0]])]});}
            var Q63;
            {var subQ0=sQuery(id+"F0.wireOp",EDGE,"yqfY02yN-hyVq-32UO-ZW3n-jwWNOL1hSBTT");var subQ1=sQuery(id+"F0.wireOp",EDGE,"E4");var subQ2=makeQuery(id+"F0.imprint","INTERSECT",VERTEX,{"derivedFrom":[subQ1,subQ0]});Q63=makeQuery(id+"F0.imprint","IMPRINT",FACE,{"disambiguationData":[TD([[makeQuery(id+"F0.imprint","IMPRINT",EDGE,{"disambiguationData":[TD([[subQ2,1.0]])],"derivedFrom":subQ1}),-1.0]])]});}
            var Q64;
            {var subQ0=sQuery(id+"F0.wireOp",EDGE,"Okv4lNKS-qbql-g7VV-lbg5-xwRJb0XAX9qC");var subQ1=sQuery(id+"F0.wireOp",EDGE,"CX13CTTp-Oqm4-u2hn-fSbW-toaxqpDcd6P2");var subQ2=makeQuery(id+"F0.imprint","INTERSECT",VERTEX,{"derivedFrom":[subQ1,subQ0]});Q64=makeQuery(id+"F0.imprint","IMPRINT",FACE,{"disambiguationData":[TD([[makeQuery(id+"F0.imprint","IMPRINT",EDGE,{"disambiguationData":[TD([[subQ2,-1.0]])],"derivedFrom":subQ1}),1.0]])]});}
            var Q65;
            {var subQ0=sQuery(id+"F0.wireOp",EDGE,"BWVHoUEd-ofww-dxFT-yNqJ-OOrmRnXLyRp3");var subQ1=sQuery(id+"F0.wireOp",EDGE,"XEESbgik-Cwhb-kf8o-8iuY-mVMpAegihUSW");var subQ2=makeQuery(id+"F0.imprint","INTERSECT",VERTEX,{"derivedFrom":[subQ1,subQ0]});Q65=makeQuery(id+"F0.imprint","IMPRINT",FACE,{"disambiguationData":[TD([[makeQuery(id+"F0.imprint","IMPRINT",EDGE,{"disambiguationData":[TD([[subQ2,-1.0]])],"derivedFrom":subQ1}),-1.0]])]});}
            var Q66;
            {var subQ0=sQuery(id+"F0.wireOp",EDGE,"XEESbgik-Cwhb-kf8o-8iuY-mVMpAegihUSW");var subQ1=sQuery(id+"F0.wireOp",EDGE,"E4");var subQ2=makeQuery(id+"F0.imprint","INTERSECT",VERTEX,{"derivedFrom":[subQ1,subQ0]});Q66=makeQuery(id+"F0.imprint","IMPRINT",FACE,{"disambiguationData":[TD([[makeQuery(id+"F0.imprint","IMPRINT",EDGE,{"disambiguationData":[TD([[subQ2,-1.0]])],"derivedFrom":subQ1}),-1.0]])]});}
            var Q67;
            {var subQ0=sQuery(id+"F0.wireOp",EDGE,"ONkRjr3D-5ST7-0iBJ-Hq3S-bNWUPIyy0om7");var subQ1=sQuery(id+"F0.wireOp",EDGE,"XEESbgik-Cwhb-kf8o-8iuY-mVMpAegihUSW");var subQ2=makeQuery(id+"F0.imprint","INTERSECT",VERTEX,{"derivedFrom":[subQ1,subQ0]});Q67=makeQuery(id+"F0.imprint","IMPRINT",FACE,{"disambiguationData":[TD([[makeQuery(id+"F0.imprint","IMPRINT",EDGE,{"disambiguationData":[TD([[subQ2,-1.0]])],"derivedFrom":subQ1}),1.0]])]});}
            var Q68;
            {var subQ0=sQuery(id+"F0.wireOp",EDGE,"BWVHoUEd-ofww-dxFT-yNqJ-OOrmRnXLyRp3");var subQ1=sQuery(id+"F0.wireOp",EDGE,"PEqbovu0-osZd-sZTq-e7nW-4YB9cD3i2QqJ");var subQ2=makeQuery(id+"F0.imprint","INTERSECT",VERTEX,{"derivedFrom":[subQ1,subQ0]});Q68=makeQuery(id+"F0.imprint","IMPRINT",FACE,{"disambiguationData":[TD([[makeQuery(id+"F0.imprint","IMPRINT",EDGE,{"disambiguationData":[TD([[subQ2,-1.0]])],"derivedFrom":subQ1}),1.0]])]});}
            var Q69;
            {var subQ0=sQuery(id+"F0.wireOp",EDGE,"XdJaFeX5-YPTi-reul-S0qf-juZpPkdLSGOt");var subQ1=sQuery(id+"F0.wireOp",EDGE,"YQxu8z3E-p7so-N4Wg-IzPX-PEhLxJgFoJVr");var subQ2=makeQuery(id+"F0.imprint","INTERSECT",VERTEX,{"derivedFrom":[subQ1,subQ0]});Q69=makeQuery(id+"F0.imprint","IMPRINT",FACE,{"disambiguationData":[TD([[makeQuery(id+"F0.imprint","IMPRINT",EDGE,{"disambiguationData":[TD([[subQ2,-1.0]])],"derivedFrom":subQ1}),1.0]])]});}
            var Q70;
            {var subQ0=sQuery(id+"F0.wireOp",EDGE,"PEqbovu0-osZd-sZTq-e7nW-4YB9cD3i2QqJ");var subQ1=sQuery(id+"F0.wireOp",EDGE,"E1");var subQ2=makeQuery(id+"F0.imprint","INTERSECT",VERTEX,{"derivedFrom":[subQ1,subQ0]});Q70=makeQuery(id+"F0.imprint","IMPRINT",FACE,{"disambiguationData":[TD([[makeQuery(id+"F0.imprint","IMPRINT",EDGE,{"disambiguationData":[TD([[subQ2,-1.0]])],"derivedFrom":subQ1}),-1.0]])]});}
            var Q71;
            {var subQ0=sQuery(id+"F0.wireOp",EDGE,"BWVHoUEd-ofww-dxFT-yNqJ-OOrmRnXLyRp3");var subQ1=sQuery(id+"F0.wireOp",EDGE,"XEESbgik-Cwhb-kf8o-8iuY-mVMpAegihUSW");var subQ2=makeQuery(id+"F0.imprint","INTERSECT",VERTEX,{"derivedFrom":[subQ1,subQ0]});Q71=makeQuery(id+"F0.imprint","IMPRINT",FACE,{"disambiguationData":[TD([[makeQuery(id+"F0.imprint","IMPRINT",EDGE,{"disambiguationData":[TD([[subQ2,-1.0]])],"derivedFrom":subQ1}),1.0]])]});}
            var Q72;
            {var subQ1=sQuery(id+"F0.wireOp",EDGE,"E1");var subQ5=sQuery(id+"F0.wireOp",EDGE,"nOc6ndhr-CEWs-2MWZ-xoqL-Ha6ft26fFmGs");var subQ6=makeQuery(id+"F0.imprint","INTERSECT",VERTEX,{"derivedFrom":[subQ1,subQ5]});Q72=makeQuery(id+"F0.imprint","IMPRINT",FACE,{"disambiguationData":[TD([[makeQuery(id+"F0.imprint","IMPRINT",EDGE,{"disambiguationData":[TD([[subQ6,1.0]])],"derivedFrom":subQ1}),-1.0]])]});}
            var Q73;
            {var subQ0=sQuery(id+"F0.wireOp",EDGE,"8BRhcVoK-4ZSY-d9QQ-jCl1-HMr4gjxtuWuF");var subQ1=sQuery(id+"F0.wireOp",EDGE,"CX13CTTp-Oqm4-u2hn-fSbW-toaxqpDcd6P2");var subQ2=makeQuery(id+"F0.imprint","INTERSECT",VERTEX,{"derivedFrom":[subQ1,subQ0]});Q73=makeQuery(id+"F0.imprint","IMPRINT",FACE,{"disambiguationData":[TD([[makeQuery(id+"F0.imprint","IMPRINT",EDGE,{"disambiguationData":[TD([[subQ2,-1.0]])],"derivedFrom":subQ1}),1.0]])]});}
            var Q74;
            {var subQ0=sQuery(id+"F0.wireOp",EDGE,"XdJaFeX5-YPTi-reul-S0qf-juZpPkdLSGOt");var subQ1=sQuery(id+"F0.wireOp",EDGE,"yqfY02yN-hyVq-32UO-ZW3n-jwWNOL1hSBTT");var subQ2=makeQuery(id+"F0.imprint","INTERSECT",VERTEX,{"derivedFrom":[subQ1,subQ0]});Q74=makeQuery(id+"F0.imprint","IMPRINT",FACE,{"disambiguationData":[TD([[makeQuery(id+"F0.imprint","IMPRINT",EDGE,{"disambiguationData":[TD([[subQ2,-1.0]])],"derivedFrom":subQ1}),1.0]])]});}
            var Q75;
            {var subQ0=sQuery(id+"F0.wireOp",EDGE,"gvejoAXR-BtHd-F8Sq-gFUB-eTjeAkh79I8N");var subQ1=sQuery(id+"F0.wireOp",EDGE,"XEESbgik-Cwhb-kf8o-8iuY-mVMpAegihUSW");var subQ2=makeQuery(id+"F0.imprint","INTERSECT",VERTEX,{"derivedFrom":[subQ1,subQ0]});Q75=makeQuery(id+"F0.imprint","IMPRINT",FACE,{"disambiguationData":[TD([[makeQuery(id+"F0.imprint","IMPRINT",EDGE,{"disambiguationData":[TD([[subQ2,-1.0]])],"derivedFrom":subQ1}),1.0]])]});}
            var Q76;
            {var subQ0=sQuery(id+"F0.wireOp",EDGE,"ATKICQp3-aMIP-nDqe-qzJb-LSgsvSxOWsnF");var subQ1=sQuery(id+"F0.wireOp",EDGE,"PEqbovu0-osZd-sZTq-e7nW-4YB9cD3i2QqJ");var subQ2=makeQuery(id+"F0.imprint","INTERSECT",VERTEX,{"derivedFrom":[subQ1,subQ0]});Q76=makeQuery(id+"F0.imprint","IMPRINT",FACE,{"disambiguationData":[TD([[makeQuery(id+"F0.imprint","IMPRINT",EDGE,{"disambiguationData":[TD([[subQ2,-1.0]])],"derivedFrom":subQ1}),1.0]])]});}
            var Q77;
            {var subQ0=sQuery(id+"F0.wireOp",EDGE,"BWVHoUEd-ofww-dxFT-yNqJ-OOrmRnXLyRp3");var subQ1=sQuery(id+"F0.wireOp",EDGE,"V6lheY5w-4WYN-of84-aoai-MSi1px95FpYR");var subQ2=makeQuery(id+"F0.imprint","INTERSECT",VERTEX,{"derivedFrom":[subQ1,subQ0]});Q77=makeQuery(id+"F0.imprint","IMPRINT",FACE,{"disambiguationData":[TD([[makeQuery(id+"F0.imprint","IMPRINT",EDGE,{"disambiguationData":[TD([[subQ2,-1.0]])],"derivedFrom":subQ1}),1.0]])]});}
            var Q78;
            {var subQ0=sQuery(id+"F0.wireOp",EDGE,"fXT5uzoG-60Do-cvdt-QS0y-XCeuEJHzKh4q");var subQ1=sQuery(id+"F0.wireOp",EDGE,"E1");var subQ2=makeQuery(id+"F0.imprint","INTERSECT",VERTEX,{"derivedFrom":[subQ1,subQ0]});Q78=makeQuery(id+"F0.imprint","IMPRINT",FACE,{"disambiguationData":[TD([[makeQuery(id+"F0.imprint","IMPRINT",EDGE,{"disambiguationData":[TD([[subQ2,-1.0]])],"derivedFrom":subQ1}),-1.0]])]});}
            var Q79;
            {var subQ0=sQuery(id+"F0.wireOp",EDGE,"YQxu8z3E-p7so-N4Wg-IzPX-PEhLxJgFoJVr");var subQ1=sQuery(id+"F0.wireOp",EDGE,"E1");var subQ2=makeQuery(id+"F0.imprint","INTERSECT",VERTEX,{"derivedFrom":[subQ1,subQ0]});Q79=makeQuery(id+"F0.imprint","IMPRINT",FACE,{"disambiguationData":[TD([[makeQuery(id+"F0.imprint","IMPRINT",EDGE,{"disambiguationData":[TD([[subQ2,-1.0]])],"derivedFrom":subQ1}),-1.0]])]});}
            var Q80;
            {var subQ0=sQuery(id+"F0.wireOp",EDGE,"nOc6ndhr-CEWs-2MWZ-xoqL-Ha6ft26fFmGs");var subQ1=sQuery(id+"F0.wireOp",EDGE,"E1");var subQ2=makeQuery(id+"F0.imprint","INTERSECT",VERTEX,{"derivedFrom":[subQ1,subQ0]});Q80=makeQuery(id+"F0.imprint","IMPRINT",FACE,{"disambiguationData":[TD([[makeQuery(id+"F0.imprint","IMPRINT",EDGE,{"disambiguationData":[TD([[subQ2,-1.0]])],"derivedFrom":subQ1}),-1.0]])]});}
            var Q81;
            {var subQ0=sQuery(id+"F0.wireOp",EDGE,"yqfY02yN-hyVq-32UO-ZW3n-jwWNOL1hSBTT");var subQ1=sQuery(id+"F0.wireOp",EDGE,"E1");var subQ2=makeQuery(id+"F0.imprint","INTERSECT",VERTEX,{"derivedFrom":[subQ1,subQ0]});Q81=makeQuery(id+"F0.imprint","IMPRINT",FACE,{"disambiguationData":[TD([[makeQuery(id+"F0.imprint","IMPRINT",EDGE,{"disambiguationData":[TD([[subQ2,-1.0]])],"derivedFrom":subQ1}),-1.0]])]});}
            var Q82;
            {var subQ0=sQuery(id+"F0.wireOp",EDGE,"V6lheY5w-4WYN-of84-aoai-MSi1px95FpYR");var subQ1=sQuery(id+"F0.wireOp",EDGE,"E1");var subQ2=makeQuery(id+"F0.imprint","INTERSECT",VERTEX,{"derivedFrom":[subQ1,subQ0]});Q82=makeQuery(id+"F0.imprint","IMPRINT",FACE,{"disambiguationData":[TD([[makeQuery(id+"F0.imprint","IMPRINT",EDGE,{"disambiguationData":[TD([[subQ2,-1.0]])],"derivedFrom":subQ1}),-1.0]])]});}
            var Q83;
            {var subQ0=sQuery(id+"F0.wireOp",EDGE,"E4");var subQ1=sQuery(id+"F0.wireOp",EDGE,"E1");var subQ2=makeQuery(id+"F0.imprint","INTERSECT",VERTEX,{"derivedFrom":[subQ1,subQ0]});Q83=makeQuery(id+"F0.imprint","IMPRINT",FACE,{"disambiguationData":[TD([[makeQuery(id+"F0.imprint","IMPRINT",EDGE,{"disambiguationData":[TD([[subQ2,1.0]])],"derivedFrom":subQ1}),-1.0]])]});}
            var Q84;
            {var subQ10=sQuery(id+"F0.wireOp",EDGE,"E2");Q84=makeQuery(id+"F0.imprint","IMPRINT",FACE,{"disambiguationData":[TD([[makeQuery(id+"F0.imprint","IMPRINT",EDGE,{"derivedFrom":subQ10}),1.0]])]});}
            extrude(context, id + "F1", {"entities" : qUnion([Q0, Q1, Q2, Q3, Q4, Q5, Q6, Q7, Q8, Q9, Q10, Q11, Q12, Q13, Q14, Q15, Q16, Q17, Q18, Q19, Q20, Q21, Q22, Q23, Q24, Q25, Q26, Q27, Q28, Q29, Q30, Q31, Q32, Q33, Q34, Q35, Q36, Q37, Q38, Q39, Q40, Q41, Q42, Q43, Q44, Q45, Q46, Q47, Q48, Q49, Q50, Q51, Q52, Q53, Q54, Q55, Q56, Q57, Q58, Q59, Q60, Q61, Q62, Q63, Q64, Q65, Q66, Q67, Q68, Q69, Q70, Q71, Q72, Q73, Q74, Q75, Q76, Q77, Q78, Q79, Q80, Q81, Q82, Q83, Q84]), "depth" : 1.52 * mm});
        }
        {
            var Q0;
            Q0=makeQuery(id+"F0.imprint","IMPRINT",FACE,{"disambiguationData":[TD([[makeQuery(id+"F0.imprint","IMPRINT",EDGE,{"derivedFrom":sQuery(id+"F0.wireOp",EDGE,"E5.bottom")}),-1.0]])]});
            extrude(context, id + "F2", {"entities" : qUnion([Q0]), "operationType" : NewBodyOperationType.ADD, "depth" : 2.3 * mm});
        }
        {
            var Q0;
            Q0=makeQuery(id+"F2.opExtrude","CAP_EDGE",EDGE,{"disambiguationData":[OSD([sQuery(id+"F0.wireOp",EDGE,"E5.left")])],"isStart":false});
            var Q1;
            Q1=makeQuery(id+"F2.opExtrude","CAP_EDGE",EDGE,{"disambiguationData":[OSD([sQuery(id+"F0.wireOp",EDGE,"E5.right")])],"isStart":false});
            fillet(context, id + "F3", {"entities" : qUnion([Q0, Q1]), "radius" : 5.08 * mm, "tangentPropagation" : true, "allowEdgeOverflow" : false});
        }
    });
